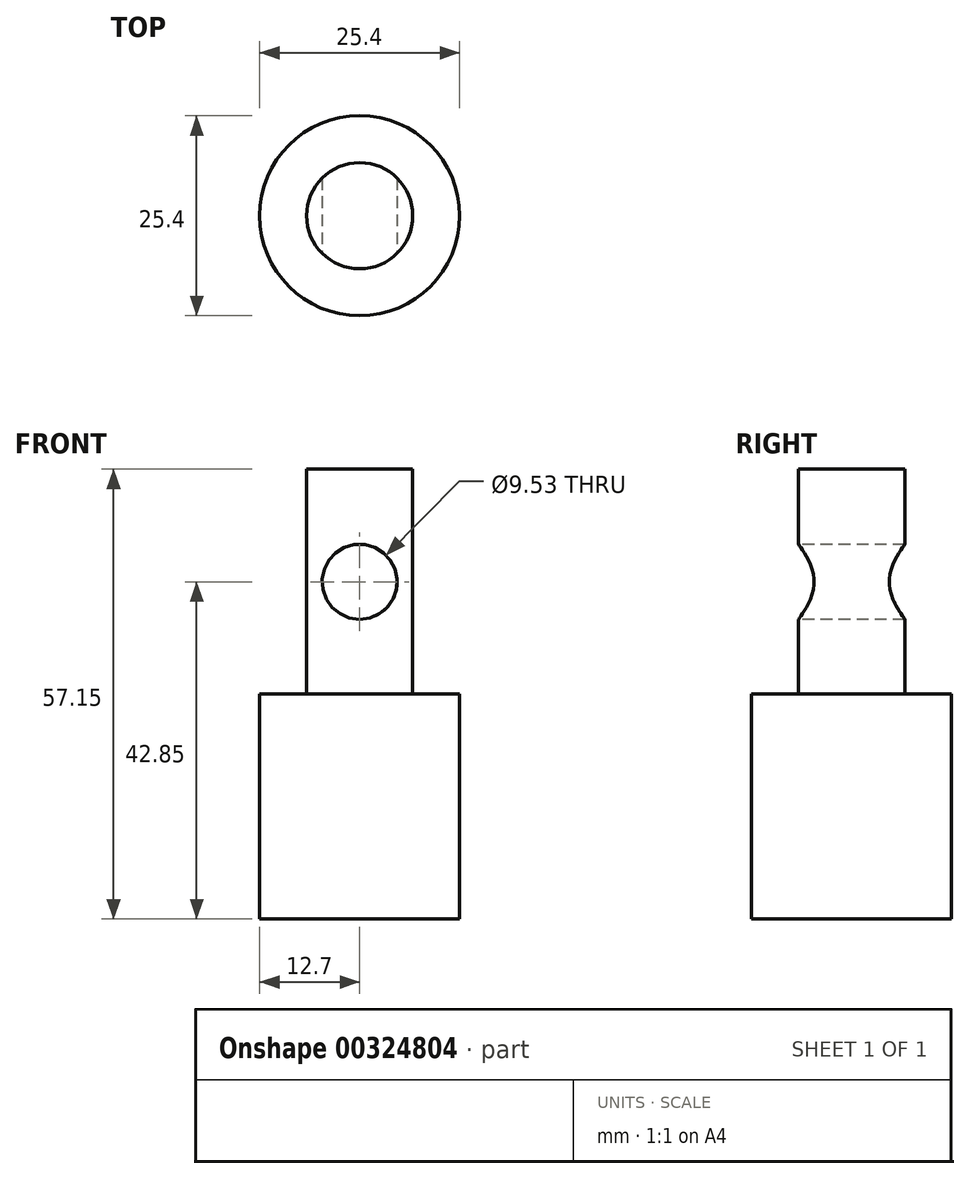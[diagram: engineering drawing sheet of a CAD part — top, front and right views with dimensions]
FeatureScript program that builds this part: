
annotation { "Feature Type Name" : "Feature", "Feature Type Description" : "" }
export const myFeature = defineFeature(function(context is Context, id is Id, definition is map)
    precondition{}
    {
        {
            var Q0;
            Q0=qCreatedBy(makeId("Top.planeOp"),FACE);
            var sketch = newSketch(context, id + "F0", { "sketchPlane" : qUnion([Q0])});
            skCircle(sketch, "E0", {"center": v(0, 0) * mm, "radius": 12.7 * mm});
            skSolve(sketch);
        }
        {
            var Q0;
            Q0=makeQuery(id+"F0.imprint","IMPRINT",FACE,{"disambiguationData":[TD([[makeQuery(id+"F0.imprint","IMPRINT",EDGE,{"derivedFrom":sQuery(id+"F0.wireOp",EDGE,"E0")}),1.0]])]});
            extrude(context, id + "F1", {"entities" : qUnion([Q0]), "depth" : 28.57 * mm, "offsetDistance" : 25.4 * mm});
        }
        {
            var Q0;
            Q0=makeQuery(id+"F1.opExtrude","CAP_FACE",FACE,{"disambiguationData":[OSD([sQuery(id+"F0.wireOp",EDGE,"E0")])],"isStart":false});
            var sketch = newSketch(context, id + "F2", { "sketchPlane" : qUnion([Q0])});
            skCircle(sketch, "E1", {"center": v(0, 0) * mm, "radius": 6.74 * mm});
            skSolve(sketch);
        }
        {
            var Q0;
            Q0=makeQuery(id+"F2.imprint","IMPRINT",FACE,{"disambiguationData":[TD([[makeQuery(id+"F2.imprint","IMPRINT",EDGE,{"derivedFrom":sQuery(id+"F2.wireOp",EDGE,"E1")}),1.0]])]});
            extrude(context, id + "F3", {"entities" : qUnion([Q0]), "operationType" : NewBodyOperationType.ADD, "depth" : 28.57 * mm, "offsetDistance" : 25.4 * mm});
        }
        {
            var Q0;
            Q0=qCreatedBy(makeId("Front.planeOp"),FACE);
            cPlane(context, id + "F4", {"entities" : qUnion([Q0]), "cplaneType" : CPlaneType.OFFSET, "offset" : 6.74 * mm, "width" : 152.4 * mm, "height" : 152.4 * mm});
        }
        {
            var Q0;
            Q0=qCreatedBy(id+"F4.planeOp",FACE);
            var sketch = newSketch(context, id + "F5", { "sketchPlane" : qUnion([Q0])});
            skCircle(sketch, "E2", {"center": v(0, 42.85) * mm, "radius": 4.76 * mm});
            skSolve(sketch);
        }
        {
            var Q0;
            Q0=makeQuery(id+"F5.imprint","IMPRINT",FACE,{"disambiguationData":[TD([[makeQuery(id+"F5.imprint","IMPRINT",EDGE,{"derivedFrom":sQuery(id+"F5.wireOp",EDGE,"E2")}),1.0]])]});
            extrude(context, id + "F6", {"entities" : qUnion([Q0]), "operationType" : NewBodyOperationType.REMOVE, "endBound" : BoundingType.THROUGH_ALL, "oppositeDirection" : true, "depth" : 25.4 * mm, "offsetDistance" : 25.4 * mm});
        }
    });
